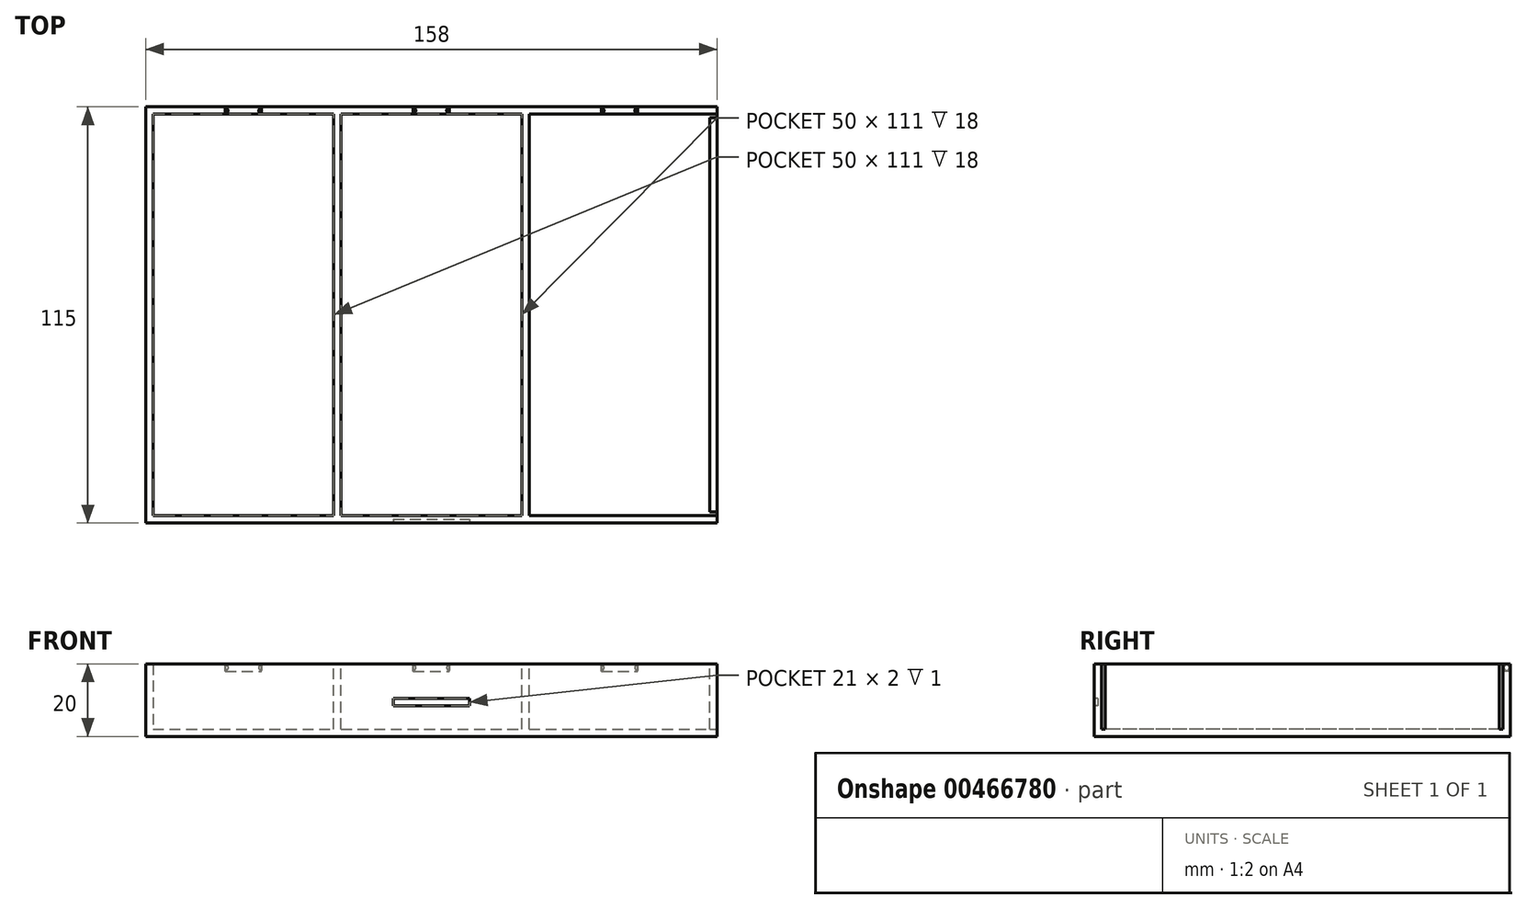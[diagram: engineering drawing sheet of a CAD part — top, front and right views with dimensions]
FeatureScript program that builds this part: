
annotation { "Feature Type Name" : "Feature", "Feature Type Description" : "" }
export const myFeature = defineFeature(function(context is Context, id is Id, definition is map)
    precondition{}
    {
        {
            var Q0;
            Q0=qCreatedBy(makeId("Top.planeOp"),FACE);
            var sketch = newSketch(context, id + "F0", { "sketchPlane" : qUnion([Q0])});
            skLineSegment(sketch, "E0.bottom", {"start": v(-119.15, 58.3) * mm, "end": v(38.85, 58.3) * mm});
            skLineSegment(sketch, "E0.top", {"start": v(-119.15, -56.7) * mm, "end": v(38.85, -56.7) * mm});
            skLineSegment(sketch, "E0.left", {"start": v(-119.15, 58.3) * mm, "end": v(-119.15, -56.7) * mm});
            skLineSegment(sketch, "E0.right", {"start": v(38.85, 58.3) * mm, "end": v(38.85, -56.7) * mm});
            skSolve(sketch);
        }
        {
            var Q0;
            Q0 = qSketchRegion(id + "F0", true);
            extrude(context, id + "F1", {"entities" : qUnion([Q0]), "depth" : 20 * mm});
        }
        {
            var Q0;
            Q0=makeQuery(id+"F1.opExtrude","CAP_FACE",FACE,{"disambiguationData":[OSD([sQuery(id+"F0.wireOp",EDGE,"E0.bottom"),sQuery(id+"F0.wireOp",EDGE,"E0.top"),sQuery(id+"F0.wireOp",EDGE,"E0.left"),sQuery(id+"F0.wireOp",EDGE,"E0.right")])],"isStart":false});
            shell(context, id + "F2", {"entities" : qUnion([Q0]), "thickness" : 2 * mm});
        }
        {
            var Q0;
            Q0=makeQuery(id+"F1.opExtrude","CAP_FACE",FACE,{"disambiguationData":[OSD([sQuery(id+"F0.wireOp",EDGE,"E0.bottom"),sQuery(id+"F0.wireOp",EDGE,"E0.top"),sQuery(id+"F0.wireOp",EDGE,"E0.left"),sQuery(id+"F0.wireOp",EDGE,"E0.right")])],"isStart":false});
            var sketch = newSketch(context, id + "F3", { "sketchPlane" : qUnion([Q0])});
            skLineSegment(sketch, "E1.bottom", {"start": v(-67.15, 58.3) * mm, "end": v(-65.15, 58.3) * mm});
            skLineSegment(sketch, "E1.top", {"start": v(-67.15, -56.7) * mm, "end": v(-65.15, -56.7) * mm});
            skLineSegment(sketch, "E1.left", {"start": v(-67.15, 58.3) * mm, "end": v(-67.15, -56.7) * mm});
            skLineSegment(sketch, "E1.right", {"start": v(-65.15, 58.3) * mm, "end": v(-65.15, -56.7) * mm});
            skLineSegment(sketch, "E2.bottom", {"start": v(-15.15, 58.3) * mm, "end": v(-13.15, 58.3) * mm});
            skLineSegment(sketch, "E2.top", {"start": v(-15.15, -56.7) * mm, "end": v(-13.15, -56.7) * mm});
            skLineSegment(sketch, "E2.left", {"start": v(-15.15, 58.3) * mm, "end": v(-15.15, -56.7) * mm});
            skLineSegment(sketch, "E2.right", {"start": v(-13.15, 58.3) * mm, "end": v(-13.15, -56.7) * mm});
            skSolve(sketch);
        }
        {
            var Q0;
            {var subQ0=sQuery(id+"F3.wireOp",EDGE,"E1.bottom");Q0=makeQuery(id+"F3.imprint","IMPRINT",FACE,{"disambiguationData":[TD([[makeQuery(id+"F3.imprint","IMPRINT",EDGE,{"derivedFrom":subQ0}),-1.0]])]});}
            var Q1;
            {var subQ0=sQuery(id+"F3.wireOp",EDGE,"E1.top");Q1=makeQuery(id+"F3.imprint","IMPRINT",FACE,{"disambiguationData":[TD([[makeQuery(id+"F3.imprint","IMPRINT",EDGE,{"derivedFrom":subQ0}),1.0]])]});}
            var Q2;
            {var subQ0=sQuery(id+"F3.wireOp",EDGE,"E2.bottom");Q2=makeQuery(id+"F3.imprint","IMPRINT",FACE,{"disambiguationData":[TD([[makeQuery(id+"F3.imprint","IMPRINT",EDGE,{"derivedFrom":subQ0}),-1.0]])]});}
            var Q3;
            {var subQ0=sQuery(id+"F3.wireOp",EDGE,"E2.top");Q3=makeQuery(id+"F3.imprint","IMPRINT",FACE,{"disambiguationData":[TD([[makeQuery(id+"F3.imprint","IMPRINT",EDGE,{"derivedFrom":subQ0}),1.0]])]});}
            var Q4;
            {var subQ0=sQuery(id+"F3.wireOp",EDGE,"E2.left");var subQ1=sQuery(id+"F0.wireOp",EDGE,"E0.bottom");var subQ2=makeQuery(id+"F2.opShell","OFFSET_EDGE",EDGE,{"disambiguationData":[OSD([subQ1]),TDD([makeQuery(id+"F1.opExtrude","CAP_EDGE",EDGE,{"disambiguationData":[OSD([subQ1])],"isStart":false})])]});var subQ3=makeQuery(id+"F3.imprint","INTERSECT",VERTEX,{"derivedFrom":[subQ2,subQ0]});Q4=makeQuery(id+"F3.imprint","IMPRINT",FACE,{"disambiguationData":[TD([[makeQuery(id+"F3.imprint","IMPRINT",EDGE,{"disambiguationData":[TD([[subQ3,-1.0]])],"derivedFrom":subQ0}),1.0]])]});}
            var Q5;
            {var subQ0=sQuery(id+"F3.wireOp",EDGE,"E1.left");var subQ1=sQuery(id+"F0.wireOp",EDGE,"E0.bottom");var subQ2=makeQuery(id+"F2.opShell","OFFSET_EDGE",EDGE,{"disambiguationData":[OSD([subQ1]),TDD([makeQuery(id+"F1.opExtrude","CAP_EDGE",EDGE,{"disambiguationData":[OSD([subQ1])],"isStart":false})])]});var subQ3=makeQuery(id+"F3.imprint","INTERSECT",VERTEX,{"derivedFrom":[subQ2,subQ0]});Q5=makeQuery(id+"F3.imprint","IMPRINT",FACE,{"disambiguationData":[TD([[makeQuery(id+"F3.imprint","IMPRINT",EDGE,{"disambiguationData":[TD([[subQ3,-1.0]])],"derivedFrom":subQ0}),1.0]])]});}
            extrude(context, id + "F4", {"entities" : qUnion([Q0, Q1, Q2, Q3, Q4, Q5]), "operationType" : NewBodyOperationType.ADD, "oppositeDirection" : true, "depth" : 20 * mm});
        }
        {
            var Q0;
            Q0=makeQuery(id+"F4.boolean.opBoolean","MERGE",FACE,{"derivedFrom":[makeQuery(id+"F1.opExtrude","CAP_FACE",FACE,{"disambiguationData":[OSD([sQuery(id+"F0.wireOp",EDGE,"E0.bottom"),sQuery(id+"F0.wireOp",EDGE,"E0.top"),sQuery(id+"F0.wireOp",EDGE,"E0.left"),sQuery(id+"F0.wireOp",EDGE,"E0.right")])],"isStart":false}),makeQuery(id+"F4.opExtrude","CAP_FACE",FACE,{"disambiguationData":[OSD([sQuery(id+"F3.wireOp",EDGE,"E1.bottom"),sQuery(id+"F3.wireOp",EDGE,"E1.top"),sQuery(id+"F3.wireOp",EDGE,"E1.left"),sQuery(id+"F3.wireOp",EDGE,"E1.right")])],"isStart":true}),makeQuery(id+"F4.opExtrude","CAP_FACE",FACE,{"disambiguationData":[OSD([sQuery(id+"F3.wireOp",EDGE,"E2.bottom"),sQuery(id+"F3.wireOp",EDGE,"E2.top"),sQuery(id+"F3.wireOp",EDGE,"E2.left"),sQuery(id+"F3.wireOp",EDGE,"E2.right")])],"isStart":true})]});
            var sketch = newSketch(context, id + "F5", { "sketchPlane" : qUnion([Q0])});
            skLineSegment(sketch, "E3.bottom", {"start": v(36.85, 56.3) * mm, "end": v(38.85, 56.3) * mm});
            skLineSegment(sketch, "E3.top", {"start": v(36.85, 55.3) * mm, "end": v(38.85, 55.3) * mm});
            skLineSegment(sketch, "E3.left", {"start": v(36.85, 56.3) * mm, "end": v(36.85, 55.3) * mm});
            skLineSegment(sketch, "E3.right", {"start": v(38.85, 56.3) * mm, "end": v(38.85, 55.3) * mm});
            skLineSegment(sketch, "E4.bottom", {"start": v(36.85, -54.7) * mm, "end": v(38.85, -54.7) * mm});
            skLineSegment(sketch, "E4.top", {"start": v(36.85, -53.7) * mm, "end": v(38.85, -53.7) * mm});
            skLineSegment(sketch, "E4.left", {"start": v(36.85, -54.7) * mm, "end": v(36.85, -53.7) * mm});
            skLineSegment(sketch, "E4.right", {"start": v(38.85, -54.7) * mm, "end": v(38.85, -53.7) * mm});
            skSolve(sketch);
        }
        {
            var Q0;
            Q0 = qSketchRegion(id + "F5", true);
            extrude(context, id + "F6", {"entities" : qUnion([Q0]), "operationType" : NewBodyOperationType.REMOVE, "oppositeDirection" : true, "depth" : 18 * mm});
        }
        {
            var Q0;
            {var subQ0=sQuery(id+"F3.wireOp",EDGE,"E1.right");var subQ1=sQuery(id+"F3.wireOp",EDGE,"E1.left");var subQ2=sQuery(id+"F0.wireOp",EDGE,"E0.left");var subQ3=sQuery(id+"F0.wireOp",EDGE,"E0.top");var subQ4=sQuery(id+"F0.wireOp",EDGE,"E0.bottom");var subQ5=sQuery(id+"F3.wireOp",EDGE,"E2.left");var subQ6=sQuery(id+"F0.wireOp",EDGE,"E0.right");var subQ7=sQuery(id+"F3.wireOp",EDGE,"E2.right");Q0=makeQuery(id+"F6.boolean.opBoolean","SPLIT",FACE,{"disambiguationData":[TD([makeQuery(id+"F1.opExtrude","SWEPT_FACE",FACE,{"disambiguationData":[OSD([subQ4])]})])],"derivedFrom":makeQuery(id+"F4.boolean.opBoolean","MERGE",FACE,{"derivedFrom":[makeQuery(id+"F1.opExtrude","CAP_FACE",FACE,{"disambiguationData":[OSD([subQ4,subQ3,subQ2,subQ6])],"isStart":false}),makeQuery(id+"F4.opExtrude","CAP_FACE",FACE,{"disambiguationData":[OSD([sQuery(id+"F3.wireOp",EDGE,"E1.bottom"),sQuery(id+"F3.wireOp",EDGE,"E1.top"),subQ1,subQ0])],"isStart":true}),makeQuery(id+"F4.opExtrude","CAP_FACE",FACE,{"disambiguationData":[OSD([sQuery(id+"F3.wireOp",EDGE,"E2.bottom"),sQuery(id+"F3.wireOp",EDGE,"E2.top"),subQ5,subQ7])],"isStart":true})]})});}
            var sketch = newSketch(context, id + "F7", { "sketchPlane" : qUnion([Q0])});
            skLineSegment(sketch, "E5.bottom", {"start": v(-97.15, 58.3) * mm, "end": v(-87.15, 58.3) * mm});
            skLineSegment(sketch, "E5.top", {"start": v(-97.15, 56.3) * mm, "end": v(-87.15, 56.3) * mm});
            skLineSegment(sketch, "E5.left", {"start": v(-97.15, 58.3) * mm, "end": v(-97.15, 56.3) * mm});
            skLineSegment(sketch, "E5.right", {"start": v(-87.15, 58.3) * mm, "end": v(-87.15, 56.3) * mm});
            skLineSegment(sketch, "E6.bottom", {"start": v(6.85, 58.3) * mm, "end": v(16.85, 58.3) * mm});
            skLineSegment(sketch, "E6.top", {"start": v(6.85, 56.3) * mm, "end": v(16.85, 56.3) * mm});
            skLineSegment(sketch, "E6.left", {"start": v(6.85, 58.3) * mm, "end": v(6.85, 56.3) * mm});
            skLineSegment(sketch, "E6.right", {"start": v(16.85, 58.3) * mm, "end": v(16.85, 56.3) * mm});
            skPoint(sketch, "E7.right.end.orphan", {"position": v(-40.15, 56.3) * mm});
            skPoint(sketch, "E7.left.end.orphan", {"position": v(-45.15, 56.3) * mm});
            skLineSegment(sketch, "E8.bottom", {"start": v(-45.18, 58.3) * mm, "end": v(-35.18, 58.3) * mm});
            skLineSegment(sketch, "E8.top", {"start": v(-45.18, 56.3) * mm, "end": v(-35.18, 56.3) * mm});
            skLineSegment(sketch, "E8.left", {"start": v(-45.18, 58.3) * mm, "end": v(-45.18, 56.3) * mm});
            skLineSegment(sketch, "E8.right", {"start": v(-35.18, 58.3) * mm, "end": v(-35.18, 56.3) * mm});
            skSolve(sketch);
        }
        {
            var Q0;
            Q0 = qSketchRegion(id + "F7", true);
            extrude(context, id + "F8", {"entities" : qUnion([Q0]), "operationType" : NewBodyOperationType.REMOVE, "oppositeDirection" : true, "depth" : 2 * mm});
        }
        {
            var Q0;
            Q0=makeQuery(id+"F8.boolean.opBoolean","COPY",FACE,{"derivedFrom":makeQuery(id+"F8.opExtrude","SWEPT_FACE",FACE,{"disambiguationData":[OSD([sQuery(id+"F7.wireOp",EDGE,"E5.left")])]})});
            var sketch = newSketch(context, id + "F9", { "sketchPlane" : qUnion([Q0])});
            skCircle(sketch, "E9", {"center": v(57.3, 19) * mm, "radius": 0.75 * mm});
            skPoint(sketch, "E9.centerSnap0", {"position": v(57.3, 20) * mm});
            skLineSegment(sketch, "E10", {"start": v(57.64, 19.67) * mm, "end": v(56.95, 18.33) * mm});
            skSolve(sketch);
        }
        {
            var Q0;
            {var subQ0=sQuery(id+"F9.wireOp",EDGE,"E10");Q0=makeQuery(id+"F9.imprint","IMPRINT",FACE,{"disambiguationData":[TD([[makeQuery(id+"F9.imprint","IMPRINT",EDGE,{"derivedFrom":subQ0}),1.0]])]});}
            var Q1;
            Q1=sQuery(id+"F9.wireOp",EDGE,"E10");
            revolve(context, id + "F10", {"operationType" : NewBodyOperationType.ADD, "entities" : qUnion([Q0]), "axis" : qUnion([Q1]), "revolveType" : RevolveType.FULL});
        }
        {
            var Q0;
            Q0=makeQuery(id+"F8.boolean.opBoolean","COPY",FACE,{"derivedFrom":makeQuery(id+"F8.opExtrude","SWEPT_FACE",FACE,{"disambiguationData":[OSD([sQuery(id+"F7.wireOp",EDGE,"E5.right")])]})});
            var sketch = newSketch(context, id + "F11", { "sketchPlane" : qUnion([Q0])});
            skCircle(sketch, "E11", {"center": v(-57.3, 19) * mm, "radius": 0.75 * mm});
            skPoint(sketch, "E11.centerSnap0", {"position": v(-56.3, 19) * mm});
            skPoint(sketch, "E11.centerSnap1", {"position": v(-57.3, 20) * mm});
            skLineSegment(sketch, "E12", {"start": v(-58.01, 19.21) * mm, "end": v(-56.57, 18.79) * mm});
            skSolve(sketch);
        }
        {
            var Q0;
            {var subQ0=sQuery(id+"F11.wireOp",EDGE,"E12");Q0=makeQuery(id+"F11.imprint","IMPRINT",FACE,{"disambiguationData":[TD([[makeQuery(id+"F11.imprint","IMPRINT",EDGE,{"derivedFrom":subQ0}),1.0]])]});}
            var Q1;
            Q1=sQuery(id+"F11.wireOp",EDGE,"E12");
            revolve(context, id + "F12", {"operationType" : NewBodyOperationType.ADD, "entities" : qUnion([Q0]), "axis" : qUnion([Q1]), "revolveType" : RevolveType.FULL});
        }
        {
            var Q0;
            Q0=makeQuery(id+"F8.boolean.opBoolean","COPY",FACE,{"derivedFrom":makeQuery(id+"F8.opExtrude","SWEPT_FACE",FACE,{"disambiguationData":[OSD([sQuery(id+"F7.wireOp",EDGE,"E8.right")])]})});
            var sketch = newSketch(context, id + "F13", { "sketchPlane" : qUnion([Q0])});
            skCircle(sketch, "E13", {"center": v(-57.3, 19) * mm, "radius": 0.75 * mm});
            skPoint(sketch, "E13.centerSnap0", {"position": v(-56.3, 19) * mm});
            skPoint(sketch, "E13.centerSnap1", {"position": v(-57.3, 20) * mm});
            skLineSegment(sketch, "E14", {"start": v(-58.03, 19.12) * mm, "end": v(-56.55, 18.87) * mm});
            skSolve(sketch);
        }
        {
            var Q0;
            {var subQ0=sQuery(id+"F13.wireOp",EDGE,"E14");Q0=makeQuery(id+"F13.imprint","IMPRINT",FACE,{"disambiguationData":[TD([[makeQuery(id+"F13.imprint","IMPRINT",EDGE,{"derivedFrom":subQ0}),1.0]])]});}
            var Q1;
            Q1=sQuery(id+"F13.wireOp",EDGE,"E14");
            revolve(context, id + "F14", {"operationType" : NewBodyOperationType.ADD, "entities" : qUnion([Q0]), "axis" : qUnion([Q1]), "revolveType" : RevolveType.FULL});
        }
        {
            var Q0;
            Q0=makeQuery(id+"F8.boolean.opBoolean","COPY",FACE,{"derivedFrom":makeQuery(id+"F8.opExtrude","SWEPT_FACE",FACE,{"disambiguationData":[OSD([sQuery(id+"F7.wireOp",EDGE,"E8.left")])]})});
            var sketch = newSketch(context, id + "F15", { "sketchPlane" : qUnion([Q0])});
            skCircle(sketch, "E15", {"center": v(57.3, 19) * mm, "radius": 0.75 * mm});
            skPoint(sketch, "E15.centerSnap0", {"position": v(56.3, 19) * mm});
            skPoint(sketch, "E15.centerSnap1", {"position": v(57.3, 20) * mm});
            skLineSegment(sketch, "E16", {"start": v(57.68, 19.64) * mm, "end": v(56.9, 18.36) * mm});
            skSolve(sketch);
        }
        {
            var Q0;
            {var subQ0=sQuery(id+"F15.wireOp",EDGE,"E16");Q0=makeQuery(id+"F15.imprint","IMPRINT",FACE,{"disambiguationData":[TD([[makeQuery(id+"F15.imprint","IMPRINT",EDGE,{"derivedFrom":subQ0}),1.0]])]});}
            var Q1;
            Q1=sQuery(id+"F15.wireOp",EDGE,"E16");
            revolve(context, id + "F16", {"operationType" : NewBodyOperationType.ADD, "entities" : qUnion([Q0]), "axis" : qUnion([Q1]), "revolveType" : RevolveType.FULL});
        }
        {
            var Q0;
            Q0=makeQuery(id+"F8.boolean.opBoolean","COPY",FACE,{"derivedFrom":makeQuery(id+"F8.opExtrude","SWEPT_FACE",FACE,{"disambiguationData":[OSD([sQuery(id+"F7.wireOp",EDGE,"E6.left")])]})});
            var sketch = newSketch(context, id + "F17", { "sketchPlane" : qUnion([Q0])});
            skCircle(sketch, "E17", {"center": v(57.3, 19) * mm, "radius": 0.75 * mm});
            skPoint(sketch, "E17.centerSnap0", {"position": v(56.3, 19) * mm});
            skPoint(sketch, "E17.centerSnap1", {"position": v(57.3, 20) * mm});
            skLineSegment(sketch, "E18", {"start": v(57.7, 19.63) * mm, "end": v(56.88, 18.37) * mm});
            skSolve(sketch);
        }
        {
            var Q0;
            {var subQ0=sQuery(id+"F17.wireOp",EDGE,"E18");Q0=makeQuery(id+"F17.imprint","IMPRINT",FACE,{"disambiguationData":[TD([[makeQuery(id+"F17.imprint","IMPRINT",EDGE,{"derivedFrom":subQ0}),1.0]])]});}
            var Q1;
            Q1=sQuery(id+"F17.wireOp",EDGE,"E18");
            revolve(context, id + "F18", {"operationType" : NewBodyOperationType.ADD, "entities" : qUnion([Q0]), "axis" : qUnion([Q1]), "revolveType" : RevolveType.FULL});
        }
        {
            var Q0;
            Q0=makeQuery(id+"F8.boolean.opBoolean","COPY",FACE,{"derivedFrom":makeQuery(id+"F8.opExtrude","SWEPT_FACE",FACE,{"disambiguationData":[OSD([sQuery(id+"F7.wireOp",EDGE,"E6.right")])]})});
            var sketch = newSketch(context, id + "F19", { "sketchPlane" : qUnion([Q0])});
            skCircle(sketch, "E19", {"center": v(-57.3, 19) * mm, "radius": 0.75 * mm});
            skPoint(sketch, "E19.centerSnap0", {"position": v(-56.3, 19) * mm});
            skPoint(sketch, "E19.centerSnap1", {"position": v(-57.3, 20) * mm});
            skLineSegment(sketch, "E20", {"start": v(-57.83, 19.53) * mm, "end": v(-56.76, 18.47) * mm});
            skSolve(sketch);
        }
        {
            var Q0;
            {var subQ0=sQuery(id+"F19.wireOp",EDGE,"E20");Q0=makeQuery(id+"F19.imprint","IMPRINT",FACE,{"disambiguationData":[TD([[makeQuery(id+"F19.imprint","IMPRINT",EDGE,{"derivedFrom":subQ0}),1.0]])]});}
            var Q1;
            Q1=sQuery(id+"F19.wireOp",EDGE,"E20");
            revolve(context, id + "F20", {"operationType" : NewBodyOperationType.ADD, "entities" : qUnion([Q0]), "axis" : qUnion([Q1]), "revolveType" : RevolveType.FULL});
        }
        {
            var Q0;
            Q0=makeQuery(id+"F1.opExtrude","SWEPT_FACE",FACE,{"disambiguationData":[OSD([sQuery(id+"F0.wireOp",EDGE,"E0.top")])]});
            var sketch = newSketch(context, id + "F21", { "sketchPlane" : qUnion([Q0])});
            skLineSegment(sketch, "E21.bottom", {"start": v(-50.65, 10.5) * mm, "end": v(-29.65, 10.5) * mm});
            skLineSegment(sketch, "E21.top", {"start": v(-50.65, 8.5) * mm, "end": v(-29.65, 8.5) * mm});
            skLineSegment(sketch, "E21.left", {"start": v(-50.65, 10.5) * mm, "end": v(-50.65, 8.5) * mm});
            skLineSegment(sketch, "E21.right", {"start": v(-29.65, 10.5) * mm, "end": v(-29.65, 8.5) * mm});
            skSolve(sketch);
        }
        {
            var Q0;
            Q0 = qSketchRegion(id + "F21", true);
            extrude(context, id + "F22", {"entities" : qUnion([Q0]), "operationType" : NewBodyOperationType.REMOVE, "oppositeDirection" : true, "depth" : 1 * mm});
        }
    });
